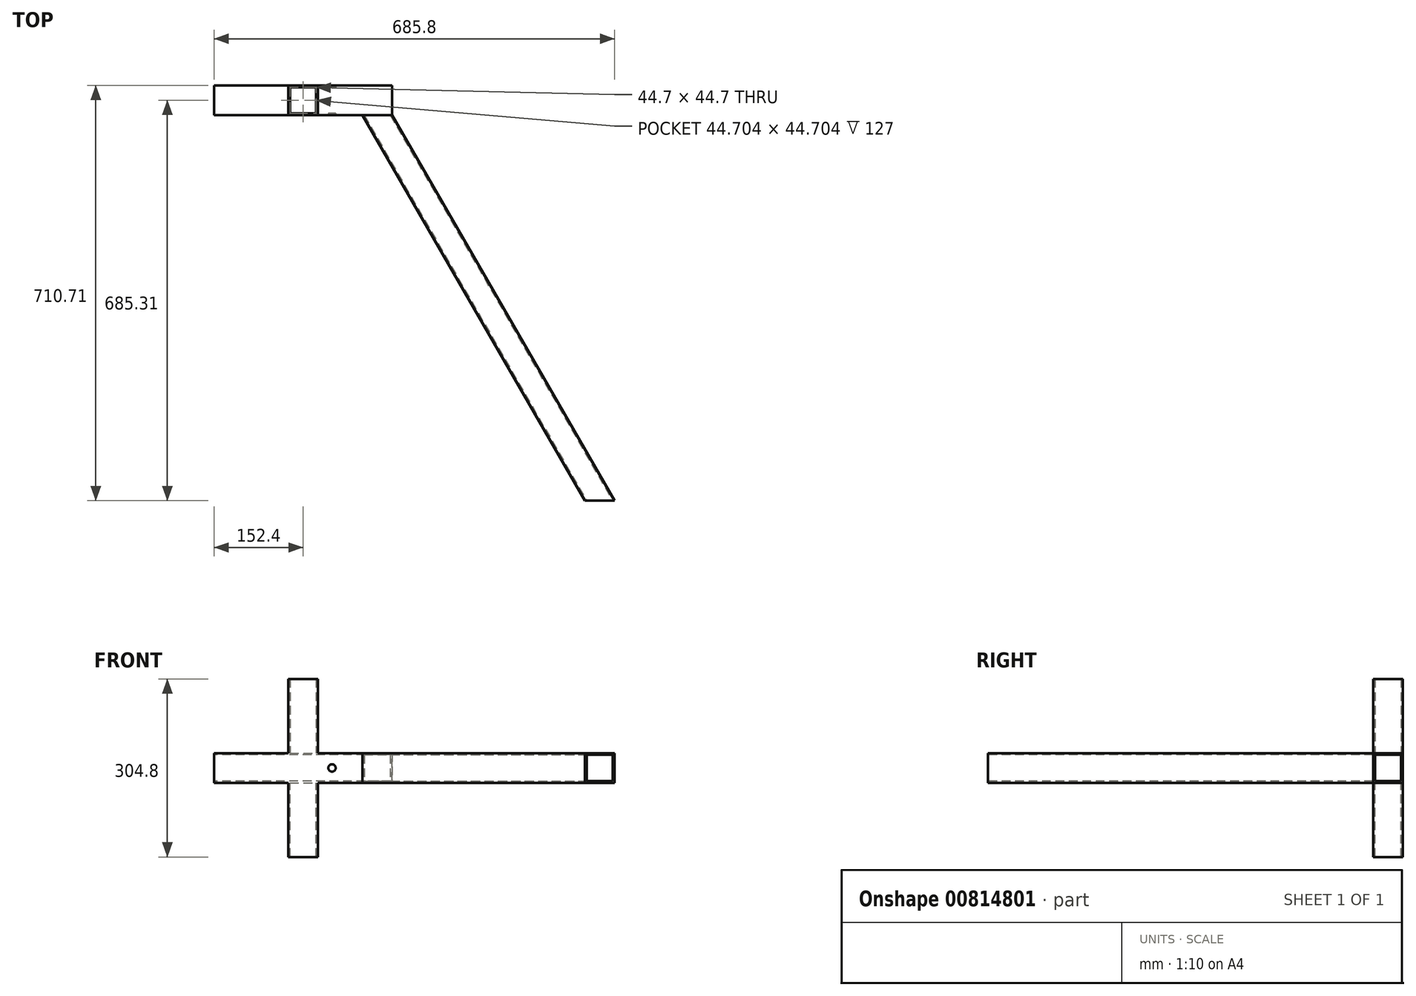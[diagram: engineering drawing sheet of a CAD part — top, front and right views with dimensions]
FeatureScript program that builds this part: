
annotation { "Feature Type Name" : "Feature", "Feature Type Description" : "" }
export const myFeature = defineFeature(function(context is Context, id is Id, definition is map)
    precondition{}
    {
        {
            var Q0;
            Q0=qCreatedBy(makeId("Right.planeOp"),FACE);
            var sketch = newSketch(context, id + "F0", { "sketchPlane" : qUnion([Q0])});
            skLineSegment(sketch, "E0.bottom", {"start": v(-25.4, 25.4) * mm, "end": v(25.4, 25.4) * mm});
            skLineSegment(sketch, "E0.top", {"start": v(-25.4, -25.4) * mm, "end": v(25.4, -25.4) * mm});
            skLineSegment(sketch, "E0.left", {"start": v(-25.4, 25.4) * mm, "end": v(-25.4, -25.4) * mm});
            skLineSegment(sketch, "E0.right", {"start": v(25.4, 25.4) * mm, "end": v(25.4, -25.4) * mm});
            skPoint(sketch, "E0.middle", {"position": v(0, 0) * mm});
            skLineSegment(sketch, "E1.bottom", {"start": v(22.35, -22.35) * mm, "end": v(-22.35, -22.35) * mm});
            skLineSegment(sketch, "E1.top", {"start": v(22.35, 22.35) * mm, "end": v(-22.35, 22.35) * mm});
            skLineSegment(sketch, "E1.left", {"start": v(22.35, -22.35) * mm, "end": v(22.35, 22.35) * mm});
            skLineSegment(sketch, "E1.right", {"start": v(-22.35, -22.35) * mm, "end": v(-22.35, 22.35) * mm});
            skSolve(sketch);
        }
        {
            var Q0;
            Q0 = qSketchRegion(id + "F0", true);
            extrude(context, id + "F1", {"entities" : qUnion([Q0]), "endBound" : BoundingType.SYMMETRIC, "depth" : 304.8 * mm, "offsetDistance" : 25.4 * mm});
        }
        {
            var Q0;
            Q0=makeQuery(id+"F1.opExtrude","SWEPT_FACE",FACE,{"disambiguationData":[OSD([sQuery(id+"F0.wireOp",EDGE,"E0.top")])]});
            var sketch = newSketch(context, id + "F2", { "sketchPlane" : qUnion([Q0])});
            skLineSegment(sketch, "E2.bottom", {"start": v(-25.4, 25.4) * mm, "end": v(25.4, 25.4) * mm});
            skLineSegment(sketch, "E2.top", {"start": v(-25.4, -25.4) * mm, "end": v(25.4, -25.4) * mm});
            skLineSegment(sketch, "E2.left", {"start": v(-25.4, 25.4) * mm, "end": v(-25.4, -25.4) * mm});
            skLineSegment(sketch, "E2.right", {"start": v(25.4, 25.4) * mm, "end": v(25.4, -25.4) * mm});
            skPoint(sketch, "E2.middle", {"position": v(0, 0) * mm});
            skLineSegment(sketch, "E3.bottom", {"start": v(-22.35, 22.35) * mm, "end": v(22.35, 22.35) * mm});
            skLineSegment(sketch, "E3.top", {"start": v(-22.35, -22.35) * mm, "end": v(22.35, -22.35) * mm});
            skLineSegment(sketch, "E3.left", {"start": v(-22.35, 22.35) * mm, "end": v(-22.35, -22.35) * mm});
            skLineSegment(sketch, "E3.right", {"start": v(22.35, 22.35) * mm, "end": v(22.35, -22.35) * mm});
            skSolve(sketch);
        }
        {
            var Q0;
            Q0 = qSketchRegion(id + "F2", true);
            extrude(context, id + "F3", {"entities" : qUnion([Q0]), "operationType" : NewBodyOperationType.ADD, "depth" : 127 * mm, "offsetDistance" : 25.4 * mm});
        }
        {
            var Q0;
            Q0=makeQuery(id+"F1.opExtrude","SWEPT_BODY",BODY,{"disambiguationData":[OSD([sQuery(id+"F0.wireOp",EDGE,"E0.bottom"),sQuery(id+"F0.wireOp",EDGE,"E0.top"),sQuery(id+"F0.wireOp",EDGE,"E0.left"),sQuery(id+"F0.wireOp",EDGE,"E0.right"),sQuery(id+"F0.wireOp",EDGE,"E1.bottom"),sQuery(id+"F0.wireOp",EDGE,"E1.top"),sQuery(id+"F0.wireOp",EDGE,"E1.left"),sQuery(id+"F0.wireOp",EDGE,"E1.right")])]});
            var Q1;
            Q1=qCreatedBy(makeId("Top.planeOp"),FACE);
            mirror(context, id + "F4", {"operationType" : NewBodyOperationType.ADD, "entities" : qUnion([Q0]), "mirrorPlane" : qUnion([Q1])});
        }
        {
            var Q0;
            {var subQ0=makeQuery(id+"F3.boolean.opBoolean","MERGE",FACE,{"derivedFrom":[makeQuery(id+"F1.opExtrude","SWEPT_FACE",FACE,{"disambiguationData":[OSD([sQuery(id+"F0.wireOp",EDGE,"E0.left")])]}),makeQuery(id+"F3.opExtrude","SWEPT_FACE",FACE,{"disambiguationData":[OSD([sQuery(id+"F2.wireOp",EDGE,"E2.bottom")])]})]});Q0=makeQuery(id+"F4.boolean.opBoolean","MERGE",FACE,{"derivedFrom":[subQ0,makeQuery(id+"F4.opPattern","COPY",FACE,{"derivedFrom":subQ0,"instanceName":"1"})]});}
            var sketch = newSketch(context, id + "F5", { "sketchPlane" : qUnion([Q0])});
            skPoint(sketch, "E4", {"position": v(49.53, 0) * mm});
            skSolve(sketch);
        }
        {
            var Q0;
            Q0=sQuery(id+"F5.wireOp",VERTEX,"E4");
            var Q1;
            Q1=makeQuery(id+"F1.opExtrude","SWEPT_BODY",BODY,{"disambiguationData":[OSD([sQuery(id+"F0.wireOp",EDGE,"E0.bottom"),sQuery(id+"F0.wireOp",EDGE,"E0.top"),sQuery(id+"F0.wireOp",EDGE,"E0.left"),sQuery(id+"F0.wireOp",EDGE,"E0.right"),sQuery(id+"F0.wireOp",EDGE,"E1.bottom"),sQuery(id+"F0.wireOp",EDGE,"E1.top"),sQuery(id+"F0.wireOp",EDGE,"E1.left"),sQuery(id+"F0.wireOp",EDGE,"E1.right")])]});
            hole(context, id + "F6", {"style" : HoleStyle.SIMPLE, "endStyle" : HoleEndStyle.THROUGH, "holeDiameter" : 12.7 * mm, "majorDiameter" : 6.35 * mm, "isTappedThrough" : true, "tappedDepth" : 12.7 * mm, "tapClearance" : 3, "locations" : qUnion([Q0]), "scope" : qUnion([Q1])});
        }
        {
            var Q0;
            {var subQ0=makeQuery(id+"F3.boolean.opBoolean","MERGE",FACE,{"derivedFrom":[makeQuery(id+"F1.opExtrude","SWEPT_FACE",FACE,{"disambiguationData":[OSD([sQuery(id+"F0.wireOp",EDGE,"E0.left")])]}),makeQuery(id+"F3.opExtrude","SWEPT_FACE",FACE,{"disambiguationData":[OSD([sQuery(id+"F2.wireOp",EDGE,"E2.bottom")])]})]});Q0=makeQuery(id+"F4.boolean.opBoolean","MERGE",FACE,{"derivedFrom":[subQ0,makeQuery(id+"F4.opPattern","COPY",FACE,{"derivedFrom":subQ0,"instanceName":"1"})]});}
            var sketch = newSketch(context, id + "F7", { "sketchPlane" : qUnion([Q0])});
            skLineSegment(sketch, "E5.bottom", {"start": v(152.4, 25.4) * mm, "end": v(101.6, 25.4) * mm});
            skLineSegment(sketch, "E5.top", {"start": v(152.4, -25.4) * mm, "end": v(101.6, -25.4) * mm});
            skLineSegment(sketch, "E5.left", {"start": v(152.4, 25.4) * mm, "end": v(152.4, -25.4) * mm});
            skLineSegment(sketch, "E5.right", {"start": v(101.6, 25.4) * mm, "end": v(101.6, -25.4) * mm});
            skLineSegment(sketch, "E6.bottom", {"start": v(149.35, 22.35) * mm, "end": v(104.65, 22.35) * mm});
            skLineSegment(sketch, "E6.top", {"start": v(149.35, -22.35) * mm, "end": v(104.65, -22.35) * mm});
            skLineSegment(sketch, "E6.left", {"start": v(149.35, 22.35) * mm, "end": v(149.35, -22.35) * mm});
            skLineSegment(sketch, "E6.right", {"start": v(104.65, 22.35) * mm, "end": v(104.65, -22.35) * mm});
            skSolve(sketch);
        }
        {
            var Q0;
            Q0=qCreatedBy(makeId("Top.planeOp"),FACE);
            var sketch = newSketch(context, id + "F8", { "sketchPlane" : qUnion([Q0])});
            skLineSegment(sketch, "E7", {"start": v(127, -25.4) * mm, "end": v(508, -685.31) * mm});
            skSolve(sketch);
        }
        {
            var Q0;
            Q0=makeQuery(id+"F7.imprint","IMPRINT",FACE,{"disambiguationData":[TD([[makeQuery(id+"F7.imprint","IMPRINT",EDGE,{"derivedFrom":sQuery(id+"F7.wireOp",EDGE,"E5.bottom")}),1.0]])]});
            var Q1;
            Q1=sQuery(id+"F8.wireOp",EDGE,"E7");
            sweep(context, id + "F9", {"profiles" : qUnion([Q0]), "path" : qUnion([Q1])});
        }
        {
            var Q0;
            Q0=qCreatedBy(makeId("Right.planeOp"),FACE);
            var sketch = newSketch(context, id + "F10", { "sketchPlane" : qUnion([Q0])});
            skLineSegment(sketch, "E8", {"start": v(0, 0) * mm, "end": v(61.7, 0) * mm, "construction": true});
            skSolve(sketch);
        }
    });
